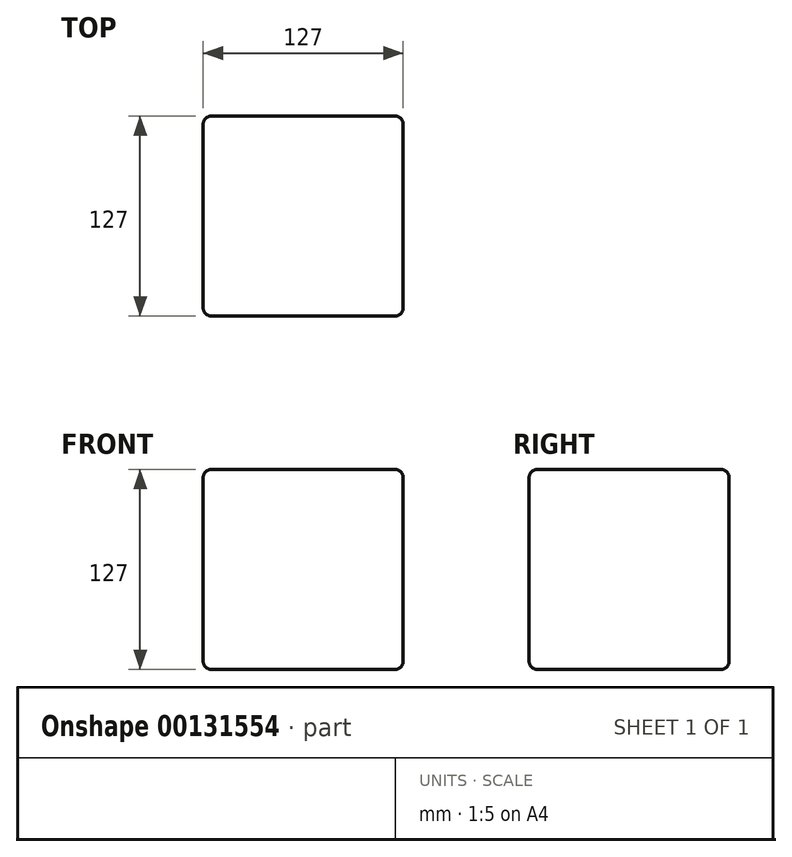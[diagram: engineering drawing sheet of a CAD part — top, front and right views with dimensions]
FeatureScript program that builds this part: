
annotation { "Feature Type Name" : "Feature", "Feature Type Description" : "" }
export const myFeature = defineFeature(function(context is Context, id is Id, definition is map)
    precondition{}
    {
        {
            var Q0;
            Q0=qCreatedBy(makeId("Front.planeOp"),FACE);
            var sketch = newSketch(context, id + "F0", { "sketchPlane" : qUnion([Q0])});
            skLineSegment(sketch, "E0.bottom", {"start": v(63.5, 63.5) * mm, "end": v(-63.5, 63.5) * mm});
            skLineSegment(sketch, "E0.top", {"start": v(63.5, -63.5) * mm, "end": v(-63.5, -63.5) * mm});
            skLineSegment(sketch, "E0.left", {"start": v(63.5, 63.5) * mm, "end": v(63.5, -63.5) * mm});
            skLineSegment(sketch, "E0.right", {"start": v(-63.5, 63.5) * mm, "end": v(-63.5, -63.5) * mm});
            skPoint(sketch, "E0.middle", {"position": v(0, 0) * mm});
            skSolve(sketch);
        }
        {
            var Q0;
            Q0 = qSketchRegion(id + "F0", true);
            extrude(context, id + "F1", {"entities" : qUnion([Q0]), "depth" : 127 * mm});
        }
        {
            var Q0;
            Q0=makeQuery(id+"F1.opExtrude","SWEPT_FACE",FACE,{"disambiguationData":[OSD([sQuery(id+"F0.wireOp",EDGE,"E0.left")])]});
            var Q1;
            Q1=makeQuery(id+"F1.opExtrude","CAP_FACE",FACE,{"disambiguationData":[OSD([sQuery(id+"F0.wireOp",EDGE,"E0.bottom"),sQuery(id+"F0.wireOp",EDGE,"E0.top"),sQuery(id+"F0.wireOp",EDGE,"E0.left"),sQuery(id+"F0.wireOp",EDGE,"E0.right")])],"isStart":false});
            var Q2;
            Q2=makeQuery(id+"F1.opExtrude","SWEPT_FACE",FACE,{"disambiguationData":[OSD([sQuery(id+"F0.wireOp",EDGE,"E0.right")])]});
            var Q3;
            Q3=makeQuery(id+"F1.opExtrude","CAP_FACE",FACE,{"disambiguationData":[OSD([sQuery(id+"F0.wireOp",EDGE,"E0.bottom"),sQuery(id+"F0.wireOp",EDGE,"E0.top"),sQuery(id+"F0.wireOp",EDGE,"E0.left"),sQuery(id+"F0.wireOp",EDGE,"E0.right")])],"isStart":true});
            var Q4;
            Q4=makeQuery(id+"F1.opExtrude","SWEPT_FACE",FACE,{"disambiguationData":[OSD([sQuery(id+"F0.wireOp",EDGE,"E0.top")])]});
            var Q5;
            Q5=makeQuery(id+"F1.opExtrude","SWEPT_FACE",FACE,{"disambiguationData":[OSD([sQuery(id+"F0.wireOp",EDGE,"E0.bottom")])]});
            fillet(context, id + "F2", {"entities" : qUnion([Q0, Q1, Q2, Q3, Q4, Q5]), "radius" : 5.08 * mm, "tangentPropagation" : true, "allowEdgeOverflow" : false});
        }
    });
